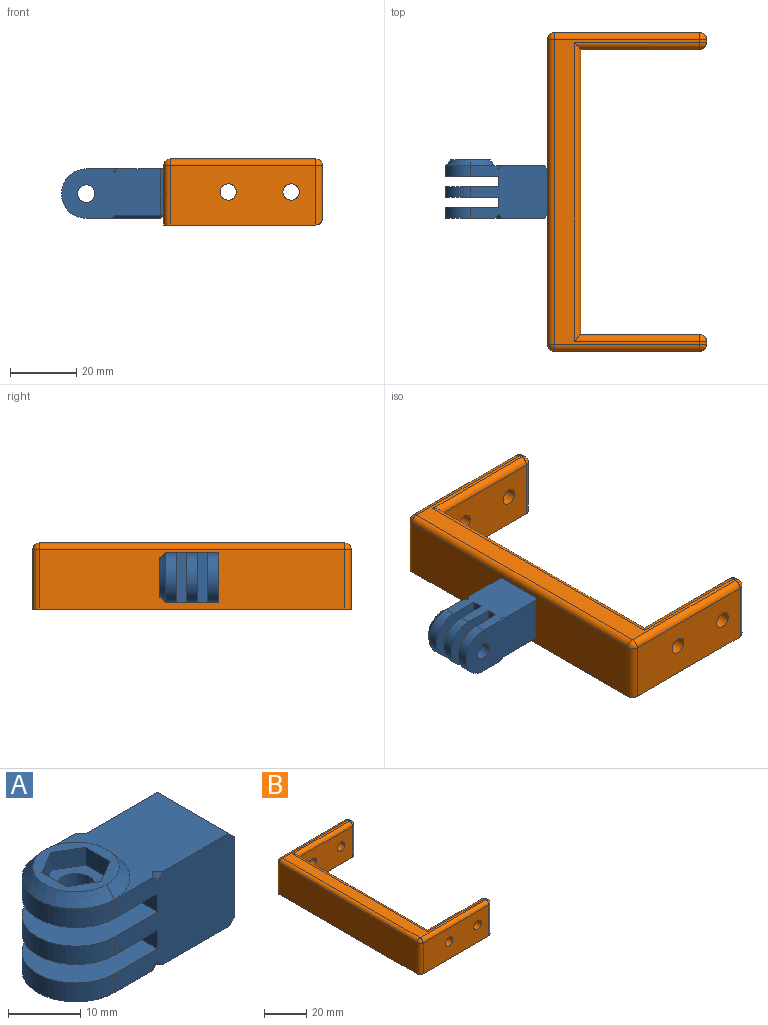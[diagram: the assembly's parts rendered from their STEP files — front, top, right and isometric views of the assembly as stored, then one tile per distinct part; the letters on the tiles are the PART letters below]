
ASSEMBLY  parts=2 mates=1
PART A: 43 faces, bbox 31x15x17.6 mm
  f0: cylinder r=7.5mm len=15mm, axis (0,0,-1), area 75.4mm2, adj f1,f3,f5,f6
  f1: plane 16x15mm, normal (0,0,1), area 193.8mm2, adj f0,f3,f5,f7,f8,f30
  f2: plane 1x1mm, normal (0.58,-0.58,-0.58), area 0.9mm2, adj f3,f6,f29
  f3: plane 23.5x15.8mm, normal (0,-1,0), area 314.8mm2, adj f0,f1,f2,f6,f9,f10,f17,f19
  f4: plane 1x1mm, normal (0.58,0.58,-0.58), area 0.9mm2, adj f5,f6,f23
  f5: plane 22.5x15.8mm, normal (0,1,0), area 272.9mm2, adj f0,f1,f4,f6,f9,f10,f18,f19
  f6: plane 30x15mm, normal (0,0,-1), area 388.3mm2, adj f0,f2,f3,f4,f5,f7,f8,f23
  f7: cylinder r=2.65mm len=5.3mm, axis (0,0,-1), area 26.6mm2, adj f1,f6,f8
  f8: cylinder r=2.65mm len=5.3mm, axis (0,0,-1), area 26.6mm2, adj f1,f6,f7
  f9: cylinder r=7.5mm len=15mm, axis (0,0,1), area 75.4mm2, adj f3,f5,f37,f40
  f10: plane 22.5x15mm, normal (0,0,1), area 233.6mm2, adj f3,f5,f17,f18,f21,f24,f28,f42
  f11: plane 4.25x3mm, normal (0.5,-0.87,0), area 14.7mm2, adj f12,f16,f36,f41
  f12: plane 4.25x3mm, normal (-0.5,-0.87,0), area 14.7mm2, adj f11,f13,f36,f41
  f13: plane 4.91x3mm, normal (-1,0,0), area 14.7mm2, adj f12,f14,f36,f41
  f14: plane 4.25x3mm, normal (-0.5,0.87,0), area 14.7mm2, adj f13,f15,f36,f41
  f15: plane 4.25x3mm, normal (0.5,0.87,0), area 14.7mm2, adj f14,f16,f36,f41
  f16: plane 4.91x3mm, normal (1,0,0), area 14.7mm2, adj f11,f15,f36,f41
  f17: plane 1x1mm, normal (0.58,-0.58,0.58), area 0.9mm2, adj f3,f10,f28
  f18: plane 1x1mm, normal (0.58,0.58,0.58), area 0.9mm2, adj f5,f10,f21
  f19: plane 15x3.15mm, normal (-1,0,0), area 47.3mm2, adj f3,f5,f32,f37
  f20: plane 14x13.8mm, normal (1,0,0), area 193.2mm2, adj f3,f22,f24,f25
  f21: plane 14x1mm, normal (0,0.71,0.71), area 19.8mm2, adj f5,f10,f18,f26
  f22: plane 13.8x1mm, normal (0.71,0.71,0), area 19.5mm2, adj f5,f20,f26,f27
  f23: plane 14x1mm, normal (0,0.71,-0.71), area 19.8mm2, adj f4,f5,f6,f27
  f24: plane 14x1mm, normal (0.71,0,0.71), area 19.8mm2, adj f3,f10,f20,f26
  f25: plane 14x1mm, normal (0.71,0,-0.71), area 19.8mm2, adj f3,f6,f20,f27
  f26: plane 1x1mm, normal (0.58,0.58,0.58), area 0.9mm2, adj f21,f22,f24
  f27: plane 1x1mm, normal (0.58,0.58,-0.58), area 0.9mm2, adj f22,f23,f25
  f28: plane 1x1mm, normal (-0.58,-0.58,0.58), area 0.9mm2, adj f3,f10,f17
  f29: plane 1x1mm, normal (-0.58,-0.58,-0.58), area 0.9mm2, adj f2,f3,f6
  f30: plane 15x3.15mm, normal (-1,0,0), area 47.3mm2, adj f1,f3,f5,f33
  f31: cylinder r=7.5mm len=15mm, axis (0,0,-1), area 73mm2, adj f3,f5,f32,f33
  f32: plane 16x15mm, normal (0,0,1), area 193.8mm2, adj f3,f5,f19,f31,f34,f35
  f33: plane 16x15mm, normal (0,0,-1), area 193.8mm2, adj f3,f5,f30,f31,f34,f35
  f34: cylinder r=2.65mm len=5.3mm, axis (0,0,-1), area 25.8mm2, adj f32,f33,f35
  f35: cylinder r=2.65mm len=5.3mm, axis (0,0,-1), area 25.8mm2, adj f32,f33,f34
  f36: plane 9.82x8.5mm, normal (0,0,1), area 40.5mm2, adj f11,f12,f13,f14,f15,f16,f38,f39
  f37: plane 16x15mm, normal (0,0,-1), area 193.8mm2, adj f3,f5,f9,f19,f38,f39
  f38: cylinder r=2.65mm len=5.3mm, axis (0,0,-1), area 16.7mm2, adj f36,f37,f39
  f39: cylinder r=2.65mm len=5.3mm, axis (0,0,-1), area 16.7mm2, adj f36,f37,f38
  f40: cone r=7.5mm half-angle=39.8deg, axis (0,0,-1), area 49.7mm2, adj f9,f41,f42
  f41: plane 12x12mm, normal (0,0,1), area 50.5mm2, adj f11,f12,f13,f14,f15,f16,f40,f42
  f42: cone r=7.5mm half-angle=39.8deg, axis (0,0,-1), area 49.7mm2, adj f10,f40,f41
PART B: 36 faces, bbox 48.1x96.5x20 mm
  f0: plane 92.5x18mm, normal (-1,0,0), area 1665mm2, adj f9,f26,f32,f35
  f1: plane 44.1x18mm, normal (0,-1,0), area 754.9mm2, adj f9,f12,f13,f29,f33,f35
  f2: plane 16x1mm, normal (1,0,0), area 16mm2, adj f22,f25,f28,f29
  f3: plane 36.1x18mm, normal (0,1,0), area 610.9mm2, adj f4,f9,f12,f13,f21,f22
  f4: plane 86.5x18mm, normal (1,0,0), area 1557mm2, adj f3,f5,f9,f18
  f5: plane 36.1x18mm, normal (0,-1,0), area 610.9mm2, adj f4,f9,f10,f11,f14,f15
  f6: plane 16x1mm, normal (1,0,0), area 16mm2, adj f14,f16,f19,f20
  f7: plane 44.1x18mm, normal (0,1,0), area 754.9mm2, adj f9,f10,f11,f19,f26,f27
  f8: plane 92.5x44.1mm, normal (0,0,1), area 631.2mm2, adj f15,f18,f20,f21,f27,f28,f32,f33
  f9: plane 96.5x46.1mm, normal (0,0,-1), area 1324.3mm2, adj f0,f1,f3,f4,f5,f7,f16,f25
  f10: cylinder r=2.49mm len=5mm, axis (0,-1,0), area 78.2mm2, adj f5,f7
  f11: cylinder r=2.49mm len=5mm, axis (0,-1,0), area 78.2mm2, adj f5,f7
  f12: cylinder r=2.49mm len=5mm, axis (0,1,0), area 78.2mm2, adj f1,f3
  f13: cylinder r=2.49mm len=5mm, axis (0,1,0), area 78.2mm2, adj f1,f3
  f14: cylinder r=2mm len=18mm, axis (0,0,-1), area 54.3mm2, adj f5,f6,f16,f17
  f15: cylinder r=2mm len=38.1mm, axis (-1,0,0), area 115.7mm2, adj f5,f8,f17,f18
  f16: cylinder r=2mm len=5mm, axis (0,1,0), area 11.1mm2, adj f6,f9,f14,f19
  f17: sphere r=2mm, area 6.3mm2, adj f14,f15,f20
  f18: cylinder r=2mm len=90.5mm, axis (0,-1,0), area 276.3mm2, adj f4,f8,f15,f21
  f19: cylinder r=2mm len=18mm, axis (0,0,-1), area 54.3mm2, adj f6,f7,f16,f23
  f20: cylinder r=2mm len=2mm, axis (0,-1,0), area 3.1mm2, adj f6,f8,f17,f23
  f21: cylinder r=2mm len=38.1mm, axis (1,0,0), area 115.7mm2, adj f3,f8,f18,f24
  f22: cylinder r=2mm len=18mm, axis (0,0,-1), area 54.3mm2, adj f2,f3,f24,f25
  f23: sphere r=2mm, area 6.3mm2, adj f19,f20,f27
  f24: sphere r=2mm, area 6.3mm2, adj f21,f22,f28
  f25: cylinder r=2mm len=5mm, axis (0,1,0), area 11.1mm2, adj f2,f9,f22,f29
  f26: cylinder r=2mm len=18mm, axis (0,0,-1), area 56.5mm2, adj f0,f7,f9,f30
  f27: cylinder r=2mm len=44.1mm, axis (1,0,0), area 138.5mm2, adj f7,f8,f23,f30
  f28: cylinder r=2mm len=2mm, axis (0,-1,0), area 3.1mm2, adj f2,f8,f24,f31
  f29: cylinder r=2mm len=18mm, axis (0,0,-1), area 54.3mm2, adj f1,f2,f25,f31
  f30: sphere r=2mm, area 6.3mm2, adj f26,f27,f32
  f31: sphere r=2mm, area 6.3mm2, adj f28,f29,f33
  f32: cylinder r=2mm len=92.5mm, axis (0,1,0), area 290.6mm2, adj f0,f8,f30,f34
  f33: cylinder r=2mm len=44.1mm, axis (-1,0,0), area 138.5mm2, adj f1,f8,f31,f34
  f34: sphere r=2mm, area 6.3mm2, adj f32,f33,f35
  f35: cylinder r=2mm len=18mm, axis (0,0,-1), area 56.5mm2, adj f0,f1,f9,f34
PLACE A rot(axis=(-1,0,0),90deg) t=(-1631.54,258.99,15.95)mm
PLACE B at identity fixed
MATE fastened A.f20 <-> B.f0  axis (1,0,0) through (62.97,261.62,10)mm
